# Revit family: Переходник компрессионные на евроконус 3-4
name_source: partatom
category: Соединительные детали трубопроводов
revit_build: Autodesk Revit 2017 (Build: 20160225_1515(x64)
units: mm (PartAtom-declared; Revit-internal decimal feet)

## family parameters
Всегда вертикально = Да
На основе рабочей плоскости = Нет
Общий = Нет
При загрузке вырезать с полостями = Нет
Размер круглого соединителя = Использовать радиус
Тип детали = Переход

## types (3) — shared parameters
ADSK_Единица измерения = шт
ADSK_Завод-изготовитель = Sanext
G = 25 мм
URL = http://sanext.ru
a = 24 мм
g = 13 мм
Изготовитель = Sanext
Материал фитинга = DZR латунь
Разработчик = ООО ПРОРУБИМ
Разработчик (телефон) = +7(495)649-85-43
Разработчик модели (URL) = http://prorubim.com
zero-valued in all types: ADSK_Масса

## per-type parameters (varying)
| type | ADSK_Код изделия | DN | R | r1 |
| Переходник компрессионный на евроконус 16×2,0/2,2-G 3/4 | 4933 | 16 мм | 8 мм | 13 мм |
| Переходник компрессионный на евроконус 20×2,8-G3/4 | 4932 | 20 мм | 10 мм | 15 мм |
| Переходник компрессионный на евроконус 20×2,0-G3/4 | 4934 | 20 мм | 10 мм | 15 мм |

note: column(s) folded — value = type name in every type: ADSK_Наименование
